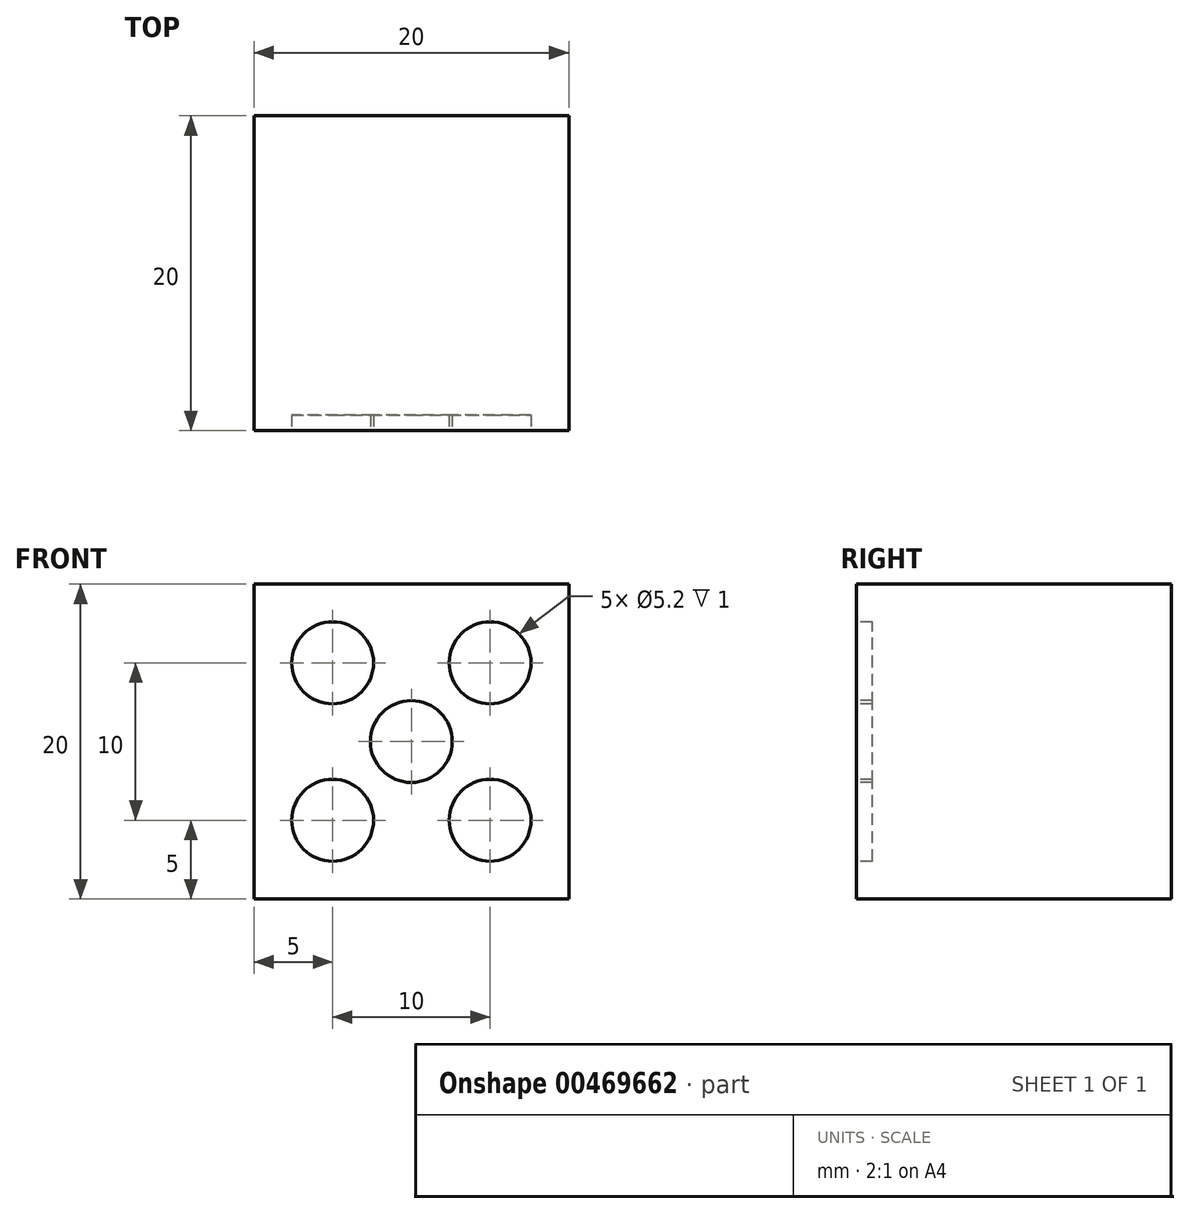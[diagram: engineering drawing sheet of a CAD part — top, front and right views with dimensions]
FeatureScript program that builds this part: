
annotation { "Feature Type Name" : "Feature", "Feature Type Description" : "" }
export const myFeature = defineFeature(function(context is Context, id is Id, definition is map)
    precondition{}
    {
        {
            var Q0;
            Q0=qCreatedBy(makeId("Front.planeOp"),FACE);
            var sketch = newSketch(context, id + "F0", { "sketchPlane" : qUnion([Q0])});
            skLineSegment(sketch, "E0.bottom", {"start": v(0, 0) * mm, "end": v(-20, 0) * mm});
            skLineSegment(sketch, "E0.top", {"start": v(0, 20) * mm, "end": v(-20, 20) * mm});
            skLineSegment(sketch, "E0.left", {"start": v(0, 0) * mm, "end": v(0, 20) * mm});
            skLineSegment(sketch, "E0.right", {"start": v(-20, 0) * mm, "end": v(-20, 20) * mm});
            skSolve(sketch);
        }
        {
            var Q0;
            Q0 = qSketchRegion(id + "F0", true);
            extrude(context, id + "F1", {"entities" : qUnion([Q0]), "depth" : 20 * mm});
        }
        {
            var Q0;
            Q0=makeQuery(id+"F1.opExtrude","CAP_FACE",FACE,{"disambiguationData":[OSD([sQuery(id+"F0.wireOp",EDGE,"E0.bottom"),sQuery(id+"F0.wireOp",EDGE,"E0.top"),sQuery(id+"F0.wireOp",EDGE,"E0.left"),sQuery(id+"F0.wireOp",EDGE,"E0.right")])],"isStart":false});
            var sketch = newSketch(context, id + "F2", { "sketchPlane" : qUnion([Q0])});
            skLineSegment(sketch, "E1", {"start": v(-20, 20) * mm, "end": v(0, 0) * mm, "construction": true});
            skLineSegment(sketch, "E2", {"start": v(0, 20) * mm, "end": v(-20, 0) * mm, "construction": true});
            skLineSegment(sketch, "E3", {"start": v(-20, 10) * mm, "end": v(0, 10) * mm, "construction": true});
            skLineSegment(sketch, "E4", {"start": v(-10, 0) * mm, "end": v(-10, 20) * mm, "construction": true});
            skCircle(sketch, "E5", {"center": v(-10, 10) * mm, "radius": 2.6 * mm});
            skCircle(sketch, "E6", {"center": v(-15, 15) * mm, "radius": 2.6 * mm});
            skLineSegment(sketch, "E7.MirrorCS", {"start": v(0, 10) * mm, "end": v(-20, 10) * mm, "construction": true});
            skCircle(sketch, "E8.MirrorC", {"center": v(-5, 15) * mm, "radius": 2.6 * mm});
            skCircle(sketch, "E9.MirrorC", {"center": v(-15, 5) * mm, "radius": 2.6 * mm});
            skCircle(sketch, "E10.MirrorC", {"center": v(-5, 5) * mm, "radius": 2.6 * mm});
            skSolve(sketch);
        }
        {
            var Q0;
            Q0 = qSketchRegion(id + "F2", true);
            extrude(context, id + "F3", {"entities" : qUnion([Q0]), "operationType" : NewBodyOperationType.REMOVE, "oppositeDirection" : true, "depth" : 1 * mm});
        }
    });
